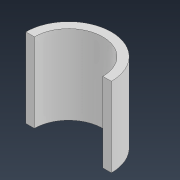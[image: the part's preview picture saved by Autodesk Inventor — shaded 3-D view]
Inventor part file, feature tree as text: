
AUTODESK INVENTOR PART (.ipt)
format: ipt  version: 2022 (Build 260153000, 153)  size: 89,088 bytes
history: native  units: mm
features: extrude x1, sketch x1
ambient origin geometry x8: Origin, YZ Plane, XZ Plane, XY Plane, X Axis, Y Axis, Z Axis, Center Point
bodies: Solid1 (feature_tree)
feature tree (2):
  extrude  "Extrusion1"  Depth=23.172mm
  sketch  "Sketch1"  dims[d0=20.0mm d1=25.0mm d2=23.172mm d3=0.0mm]
